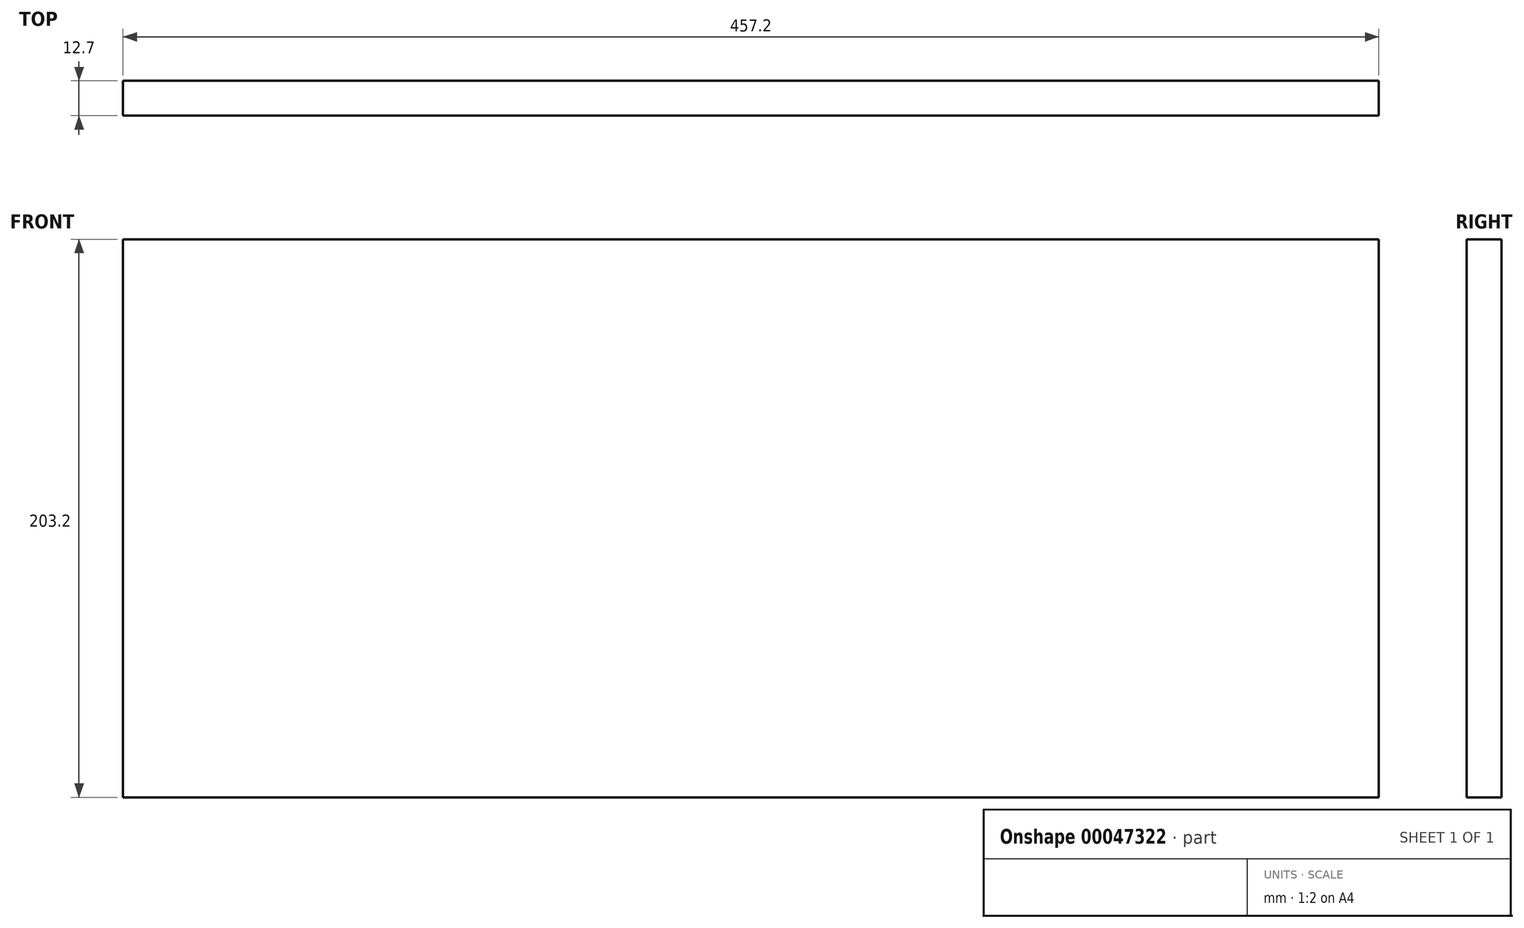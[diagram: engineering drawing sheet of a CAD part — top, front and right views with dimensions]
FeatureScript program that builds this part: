
annotation { "Feature Type Name" : "Feature", "Feature Type Description" : "" }
export const myFeature = defineFeature(function(context is Context, id is Id, definition is map)
    precondition{}
    {
        {
            var Q0;
            Q0=qCreatedBy(makeId("Front.planeOp"),FACE);
            var sketch = newSketch(context, id + "F0", { "sketchPlane" : qUnion([Q0])});
            skLineSegment(sketch, "E0.bottom", {"start": v(-227.47, -2.16) * mm, "end": v(229.73, -2.16) * mm});
            skLineSegment(sketch, "E0.top", {"start": v(-227.47, -205.36) * mm, "end": v(229.73, -205.36) * mm});
            skLineSegment(sketch, "E0.left", {"start": v(-227.47, -2.16) * mm, "end": v(-227.47, -205.36) * mm});
            skLineSegment(sketch, "E0.right", {"start": v(229.73, -2.16) * mm, "end": v(229.73, -205.36) * mm});
            skSolve(sketch);
        }
        {
            var Q0;
            Q0=makeQuery(id+"F0.imprint","IMPRINT",FACE,{"disambiguationData":[TD([[makeQuery(id+"F0.imprint","IMPRINT",EDGE,{"derivedFrom":sQuery(id+"F0.wireOp",EDGE,"E0.bottom")}),-1.0]])]});
            extrude(context, id + "F1", {"entities" : qUnion([Q0]), "depth" : 12.7 * mm});
        }
    });
